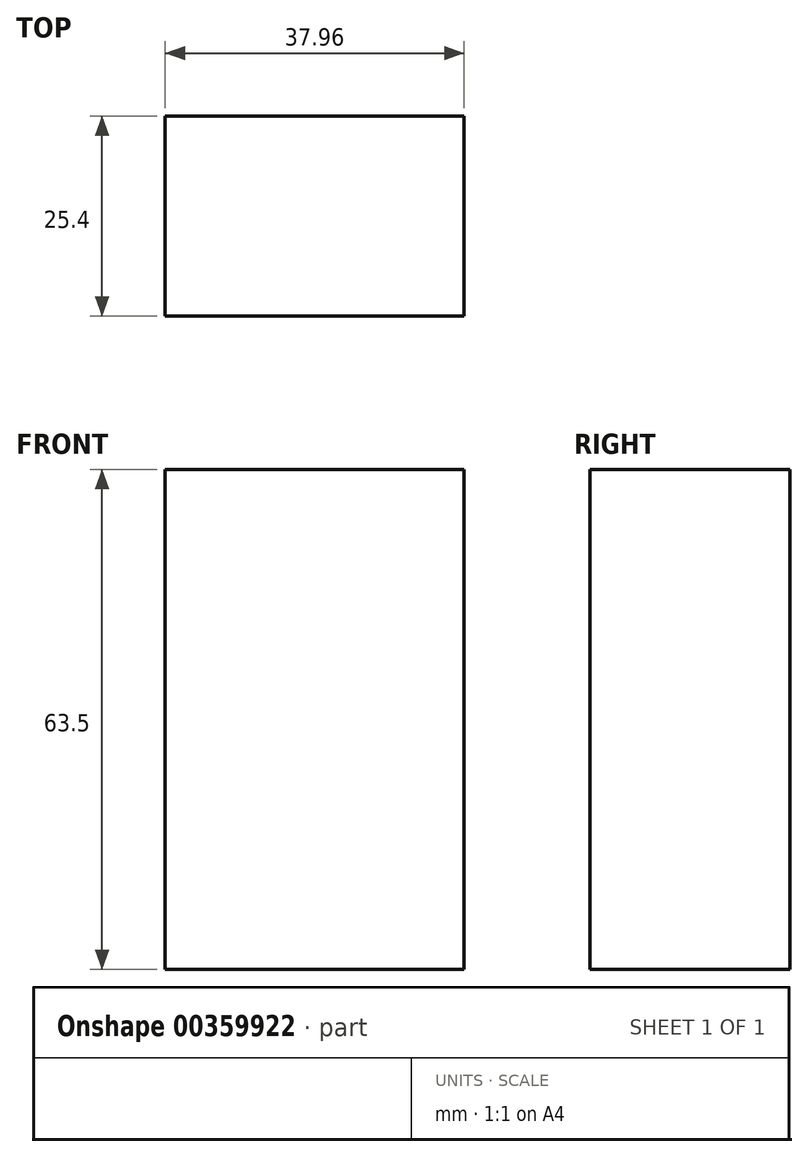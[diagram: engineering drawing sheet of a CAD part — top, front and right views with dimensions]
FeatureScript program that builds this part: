
annotation { "Feature Type Name" : "Feature", "Feature Type Description" : "" }
export const myFeature = defineFeature(function(context is Context, id is Id, definition is map)
    precondition{}
    {
        {
            var Q0;
            Q0=qCreatedBy(makeId("Front.planeOp"),FACE);
            var sketch = newSketch(context, id + "F0", { "sketchPlane" : qUnion([Q0])});
            skLineSegment(sketch, "E0.bottom", {"start": v(0, 0) * mm, "end": v(37.96, 0) * mm});
            skLineSegment(sketch, "E0.top", {"start": v(0, 63.5) * mm, "end": v(37.96, 63.5) * mm});
            skLineSegment(sketch, "E0.left", {"start": v(0, 0) * mm, "end": v(0, 63.5) * mm});
            skLineSegment(sketch, "E0.right", {"start": v(37.96, 0) * mm, "end": v(37.96, 63.5) * mm});
            skSolve(sketch);
        }
        {
            var Q0;
            Q0=makeQuery(id+"F0.imprint","IMPRINT",FACE,{"disambiguationData":[TD([[makeQuery(id+"F0.imprint","IMPRINT",EDGE,{"derivedFrom":sQuery(id+"F0.wireOp",EDGE,"E0.bottom")}),1.0]])]});
            extrude(context, id + "F1", {"entities" : qUnion([Q0]), "depth" : 25.4 * mm});
        }
    });
